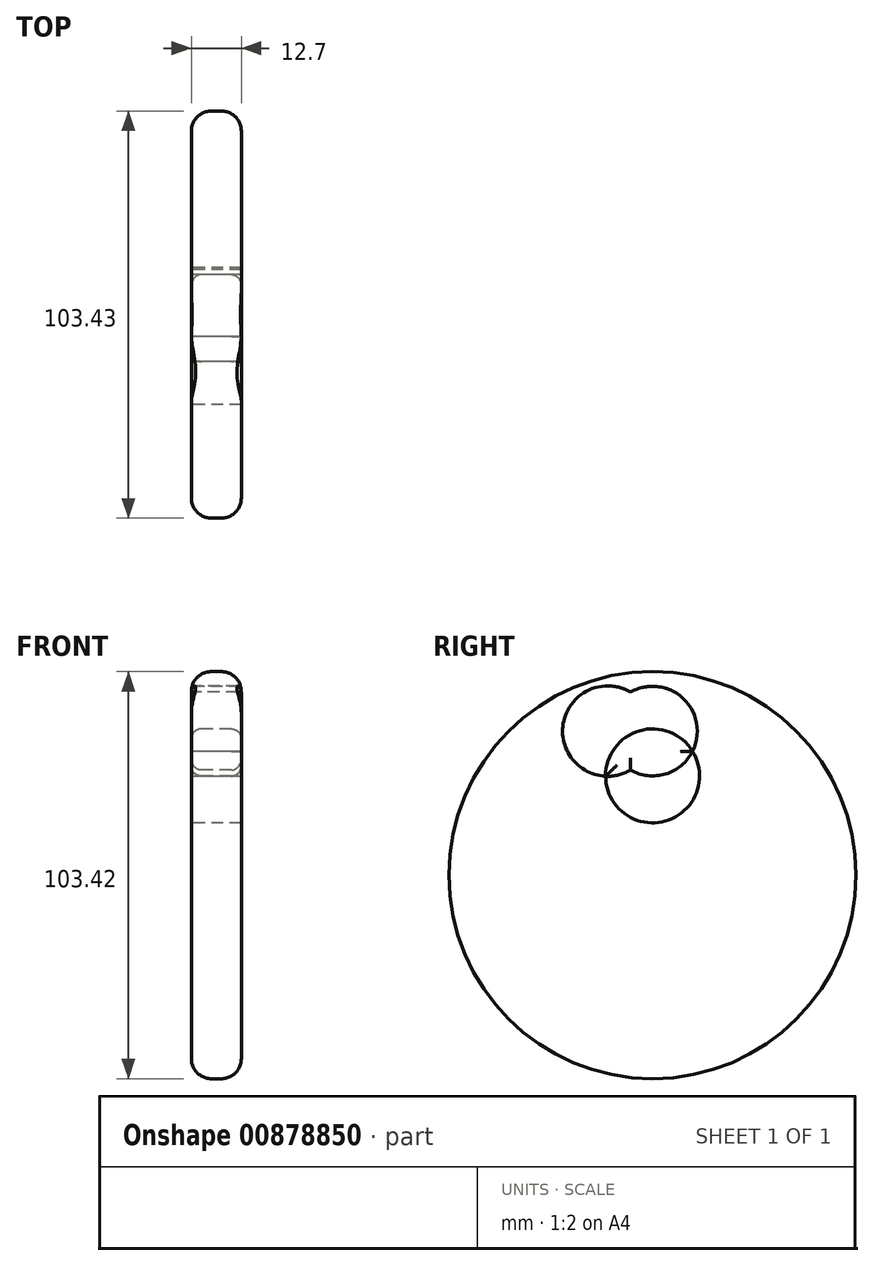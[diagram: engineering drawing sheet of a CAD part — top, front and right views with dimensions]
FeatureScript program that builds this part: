
annotation { "Feature Type Name" : "Feature", "Feature Type Description" : "" }
export const myFeature = defineFeature(function(context is Context, id is Id, definition is map)
    precondition{}
    {
        {
            var Q0;
            Q0=qCreatedBy(makeId("Right.planeOp"),FACE);
            var sketch = newSketch(context, id + "F0", { "sketchPlane" : qUnion([Q0])});
            skCircle(sketch, "E0", {"center": v(-32.36, 0) * mm, "radius": 51.71 * mm});
            skCircle(sketch, "E1", {"center": v(-43.74, 36.6) * mm, "radius": 11.48 * mm});
            skCircle(sketch, "E2", {"center": v(-32.36, 36.6) * mm, "radius": 11.38 * mm});
            skCircle(sketch, "E3", {"center": v(-32.36, 25.22) * mm, "radius": 11.94 * mm});
            skSolve(sketch);
        }
        {
            var Q0;
            Q0 = qSketchRegion(id + "F0", true);
            var Q1;
            {var subQ0=sQuery(id+"F0.wireOp",EDGE,"E3");var subQ1=sQuery(id+"F0.wireOp",EDGE,"E1");var subQ2=makeQuery(id+"F0.imprint","INTERSECT",VERTEX,{"disambiguationData":[OD(0.0)],"derivedFrom":[subQ1,subQ0]});Q1=makeQuery(id+"F0.imprint","IMPRINT",FACE,{"disambiguationData":[TD([[makeQuery(id+"F0.imprint","IMPRINT",EDGE,{"disambiguationData":[TD([[subQ2,1.0]])],"derivedFrom":subQ1}),-1.0]])]});}
            var Q2;
            {var subQ0=sQuery(id+"F0.wireOp",EDGE,"E3");var subQ1=sQuery(id+"F0.wireOp",EDGE,"E1");var subQ2=makeQuery(id+"F0.imprint","INTERSECT",VERTEX,{"disambiguationData":[OD(0.0)],"derivedFrom":[subQ1,subQ0]});Q2=makeQuery(id+"F0.imprint","IMPRINT",FACE,{"disambiguationData":[TD([[makeQuery(id+"F0.imprint","IMPRINT",EDGE,{"disambiguationData":[TD([[subQ2,1.0]])],"derivedFrom":subQ1}),1.0]])]});}
            var Q3;
            {var subQ0=sQuery(id+"F0.wireOp",EDGE,"E3");var subQ1=sQuery(id+"F0.wireOp",EDGE,"E1");var subQ2=makeQuery(id+"F0.imprint","INTERSECT",VERTEX,{"disambiguationData":[OD(1.0)],"derivedFrom":[subQ1,subQ0]});Q3=makeQuery(id+"F0.imprint","IMPRINT",FACE,{"disambiguationData":[TD([[makeQuery(id+"F0.imprint","IMPRINT",EDGE,{"disambiguationData":[TD([[subQ2,-1.0]])],"derivedFrom":subQ1}),1.0]])]});}
            var Q4;
            {var subQ0=sQuery(id+"F0.wireOp",EDGE,"E2");var subQ1=sQuery(id+"F0.wireOp",EDGE,"E1");var subQ2=makeQuery(id+"F0.imprint","INTERSECT",VERTEX,{"disambiguationData":[OD(0.0)],"derivedFrom":[subQ1,subQ0]});Q4=makeQuery(id+"F0.imprint","IMPRINT",FACE,{"disambiguationData":[TD([[makeQuery(id+"F0.imprint","IMPRINT",EDGE,{"disambiguationData":[TD([[subQ2,1.0]])],"derivedFrom":subQ1}),1.0]])]});}
            extrude(context, id + "F1", {"entities" : qUnion([Q0, Q1, Q2, Q3, Q4]), "depth" : 12.7 * mm, "offsetDistance" : 25.4 * mm});
        }
        {
            var Q0;
            Q0=makeQuery(id+"F1.opExtrude","CAP_FACE",FACE,{"disambiguationData":[OSD([sQuery(id+"F0.wireOp",EDGE,"E1"),sQuery(id+"F0.wireOp",EDGE,"E2"),sQuery(id+"F0.wireOp",EDGE,"E3")])],"isStart":true});
            var Q1;
            Q1=makeQuery(id+"F1.opExtrude","CAP_FACE",FACE,{"disambiguationData":[OSD([sQuery(id+"F0.wireOp",EDGE,"E1"),sQuery(id+"F0.wireOp",EDGE,"E2"),sQuery(id+"F0.wireOp",EDGE,"E3")])],"isStart":false});
            fillet(context, id + "F2", {"entities" : qUnion([Q0, Q1]), "radius" : 2.54 * mm, "tangentPropagation" : true, "allowEdgeOverflow" : false});
        }
        {
            var Q0;
            Q0=makeQuery(id+"F1.opExtrude","CAP_EDGE",EDGE,{"disambiguationData":[OSD([sQuery(id+"F0.wireOp",EDGE,"E0")])],"isStart":true});
            var Q1;
            Q1=makeQuery(id+"F1.opExtrude","CAP_EDGE",EDGE,{"disambiguationData":[OSD([sQuery(id+"F0.wireOp",EDGE,"E0")])],"isStart":false});
            fillet(context, id + "F3", {"entities" : qUnion([Q0, Q1]), "radius" : 5.08 * mm, "tangentPropagation" : true, "allowEdgeOverflow" : false});
        }
    });
